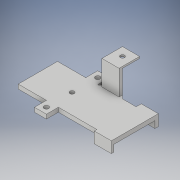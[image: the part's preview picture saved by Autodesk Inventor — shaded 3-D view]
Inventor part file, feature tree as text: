
AUTODESK INVENTOR PART (.ipt)
format: ipt  version: 2018 (Build 220112000, 112)  size: 270,336 bytes
history: native  units: in
note: dims shown in document units (in); Inventor stores cm internally (conversion verified against a paired STEP export)
features: extrude x15, sketch x15, projected_geometry x2, chamfer x1
ambient origin geometry x8: Origin, YZ Plane, XZ Plane, XY Plane, X Axis, Y Axis, Z Axis, Center Point
bodies: Solid1 (feature_tree)
feature tree (33):
  extrude  "Extrusion1"  Depth=0.3937in
  extrude  "Extrusion2"  Depth=0.0394in TaperAngle=0.0deg
  extrude  "Extrusion3"  Depth=0.0394in TaperAngle=0.0deg
  extrude  "Extrusion4"  Depth=0.6693in TaperAngle=0.0deg
  extrude  "Extrusion5"  TaperAngle=0.0deg  [1 undecoded]
  extrude  "Extrusion10"  Depth=2.2047in
  extrude  "Extrusion11"  TaperAngle=0.0deg  [1 undecoded]
  extrude  "Extrusion12"  Depth=0.7874in
  extrude  "Extrusion13"  Depth=0.7874in
  extrude  "Extrusion14"  TaperAngle=0.0deg  [1 undecoded]
  extrude  "Extrusion18"  Depth=0.2756in
  extrude  "Extrusion23"  Depth=0.2756in
  extrude  "Extrusion24"  Depth=0.1083in
  extrude  "Extrusion25"  TaperAngle=0.0deg  [1 undecoded]
  extrude  "Extrusion26"  Depth=0.3937in
  chamfer  "Chamfer1"  Distance=0.2559in
  sketch  "Sketch1"  dims[d0=0.3937in d1=0.3937in]
  sketch  "Sketch2"  dims[d2=0.1181in d3=0.0394in d4=0.0in]
  sketch  "Sketch3"  dims[d5=0.0591in d6=0.0394in d7=0.0in]
  sketch  "Sketch4"  dims[d8=0.0591in d9=0.6693in d10=0.0in]
  sketch  "Sketch5"  dims[d11=0.0591in d12=0.0in d13=0.0in]
  sketch  "Sketch11"  dims[d14=0.0591in d15=2.2047in]
  sketch  "Sketch12"  dims[d16=0.9055in d17=0.0in d42=0.0in]
  sketch  "Sketch13"  dims[d45=0.0984in d46=0.7874in]
  sketch  "Sketch14"  dims[d47=0.0394in d48=0.0in d49=0.7874in]
  sketch  "Sketch15"  dims[d50=0.0in d51=0.0in]
  sketch  "Sketch19"  dims[d52=0.2756in d53=0.2756in]
  sketch  "Sketch24"  dims[d54=0.2756in d55=0.2756in]
  sketch  "Sketch25"  dims[d56=0.1083in d57=0.1083in]
  projected_geometry  "Projected Loop2"
  sketch  "Sketch26"  dims[d58=0.0984in d59=0.0in d60=0.0in]
  sketch  "Sketch27"  dims[d61=0.1181in d62=0.3937in d63=0.2559in d64=0.0in d65=0.0394in d66=0.0in d67=0.1575in d68=0.0in d69=0.7874in d70=0.0in d80=1.1811in d81=0.0in d95=0.7874in d96=0.3937in d97=0.0787in d98=0.5709in d99=0.0in d100=0.0984in d101=0.0in d102=0.0394in d103=0.3937in d104=0.0in d105=0.0984in d106=0.3937in d107=0.0in d108=0.0787in d109=0.125in d110=45.0deg]
  projected_geometry  "Projected Loop3"
note: 4 required parameter values undecoded (feature->parameter linkage not recoverable at this tier; creation-order binding heuristic only, values carry confidence <= 0.55)
